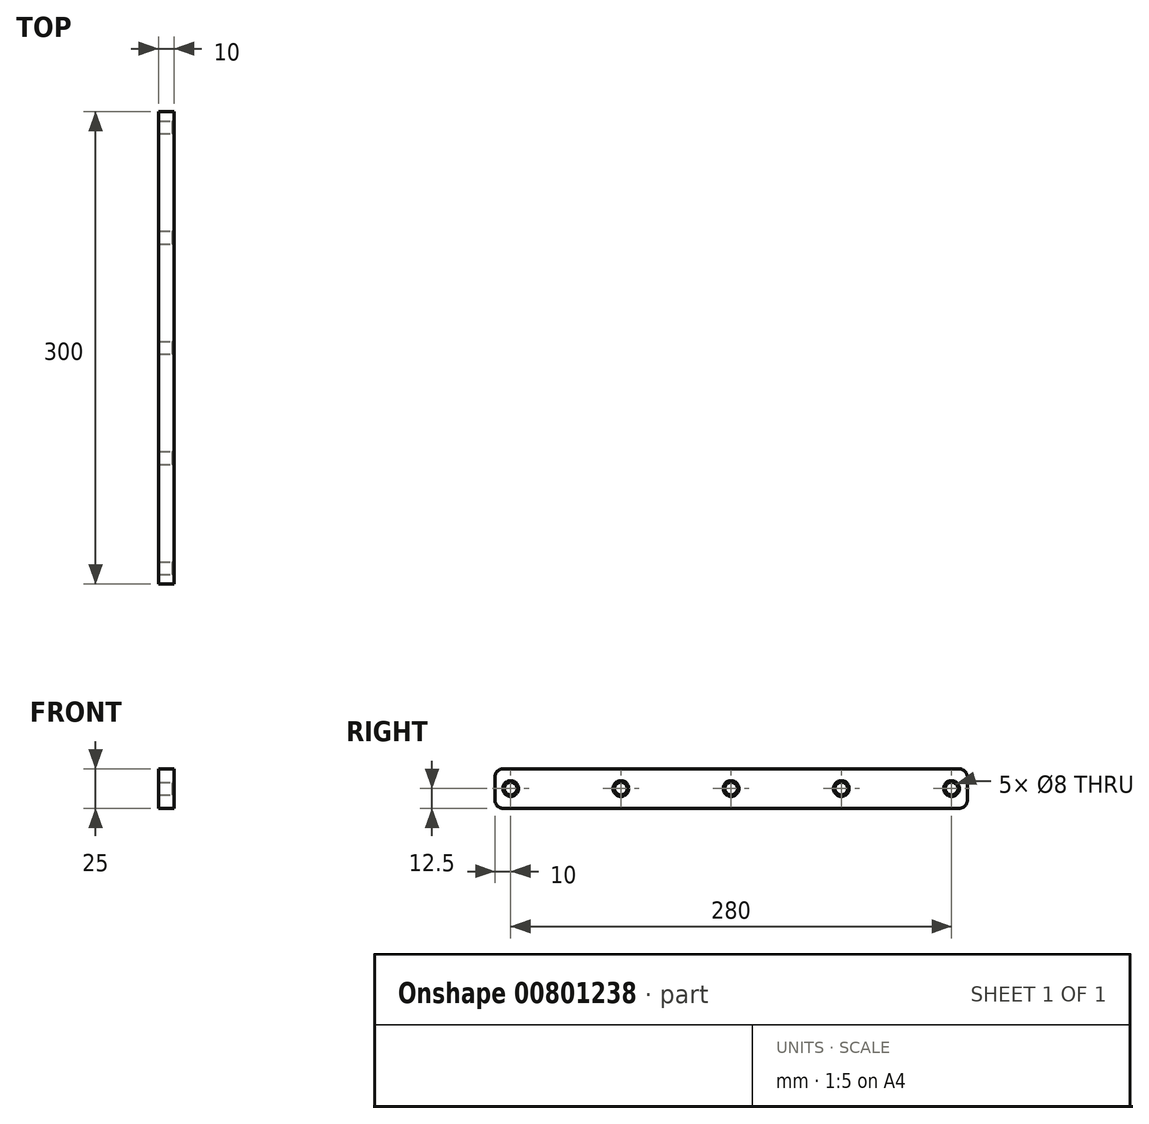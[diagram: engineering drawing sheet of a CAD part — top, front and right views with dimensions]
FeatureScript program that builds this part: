
annotation { "Feature Type Name" : "Feature", "Feature Type Description" : "" }
export const myFeature = defineFeature(function(context is Context, id is Id, definition is map)
    precondition{}
    {
        {
            var Q0;
            Q0=qCreatedBy(makeId("Top.planeOp"),FACE);
            var sketch = newSketch(context, id + "F0", { "sketchPlane" : qUnion([Q0])});
            skLineSegment(sketch, "E0.bottom", {"start": v(0, 0) * mm, "end": v(-10, 0) * mm});
            skLineSegment(sketch, "E0.top", {"start": v(0, 300) * mm, "end": v(-10, 300) * mm});
            skLineSegment(sketch, "E0.left", {"start": v(0, 0) * mm, "end": v(0, 300) * mm});
            skLineSegment(sketch, "E0.right", {"start": v(-10, 0) * mm, "end": v(-10, 300) * mm});
            skSolve(sketch);
        }
        {
            var Q0;
            Q0 = qSketchRegion(id + "F0", true);
            extrude(context, id + "F1", {"entities" : qUnion([Q0]), "depth" : 25 * mm, "offsetDistance" : 25 * mm});
        }
        {
            var Q0;
            Q0=makeQuery(id+"F1.opExtrude","SWEPT_FACE",FACE,{"disambiguationData":[OSD([sQuery(id+"F0.wireOp",EDGE,"E0.left")])]});
            var sketch = newSketch(context, id + "F2", { "sketchPlane" : qUnion([Q0])});
            skLineSegment(sketch, "E1", {"start": v(0, 12.5) * mm, "end": v(10, 12.5) * mm});
            skLineSegment(sketch, "E2", {"start": v(10, 12.5) * mm, "end": v(80, 12.5) * mm});
            skLineSegment(sketch, "E3", {"start": v(80, 12.5) * mm, "end": v(150, 12.5) * mm});
            skLineSegment(sketch, "E4", {"start": v(150, 12.5) * mm, "end": v(220, 12.5) * mm});
            skLineSegment(sketch, "E5", {"start": v(220, 12.5) * mm, "end": v(290, 12.5) * mm});
            skSolve(sketch);
        }
        {
            var Q0;
            Q0=sQuery(id+"F2.wireOp",VERTEX,"E1.end");
            var Q1;
            Q1=sQuery(id+"F2.wireOp",VERTEX,"E2.end");
            var Q2;
            Q2=sQuery(id+"F2.wireOp",VERTEX,"E3.end");
            var Q3;
            Q3=sQuery(id+"F2.wireOp",VERTEX,"E4.end");
            var Q4;
            Q4=sQuery(id+"F2.wireOp",VERTEX,"E5.end");
            var Q5;
            Q5=makeQuery(id+"F1.opExtrude","SWEPT_BODY",BODY,{"disambiguationData":[OSD([sQuery(id+"F0.wireOp",EDGE,"E0.bottom"),sQuery(id+"F0.wireOp",EDGE,"E0.top"),sQuery(id+"F0.wireOp",EDGE,"E0.left"),sQuery(id+"F0.wireOp",EDGE,"E0.right")])]});
            hole(context, id + "F3", {"style" : HoleStyle.C_SINK, "endStyle" : HoleEndStyle.THROUGH, "holeDiameter" : 8 * mm, "cSinkDiameter" : 10 * mm, "cSinkAngle" : 90 * degree, "majorDiameter" : 5 * mm, "isTappedThrough" : true, "tappedDepth" : 12 * mm, "tapClearance" : 3, "startFromSketch" : true, "locations" : qUnion([Q0, Q1, Q2, Q3, Q4]), "scope" : qUnion([Q5])});
        }
        {
            var Q0;
            Q0=makeQuery(id+"F1.opExtrude","CAP_EDGE",EDGE,{"disambiguationData":[OSD([sQuery(id+"F0.wireOp",EDGE,"E0.bottom")])],"isStart":true});
            var Q1;
            Q1=makeQuery(id+"F1.opExtrude","CAP_EDGE",EDGE,{"disambiguationData":[OSD([sQuery(id+"F0.wireOp",EDGE,"E0.top")])],"isStart":true});
            var Q2;
            Q2=makeQuery(id+"F1.opExtrude","CAP_EDGE",EDGE,{"disambiguationData":[OSD([sQuery(id+"F0.wireOp",EDGE,"E0.bottom")])],"isStart":false});
            var Q3;
            Q3=makeQuery(id+"F1.opExtrude","CAP_EDGE",EDGE,{"disambiguationData":[OSD([sQuery(id+"F0.wireOp",EDGE,"E0.top")])],"isStart":false});
            fillet(context, id + "F4", {"entities" : qUnion([Q0, Q1, Q2, Q3]), "radius" : 5 * mm, "tangentPropagation" : true, "allowEdgeOverflow" : false});
        }
    });
